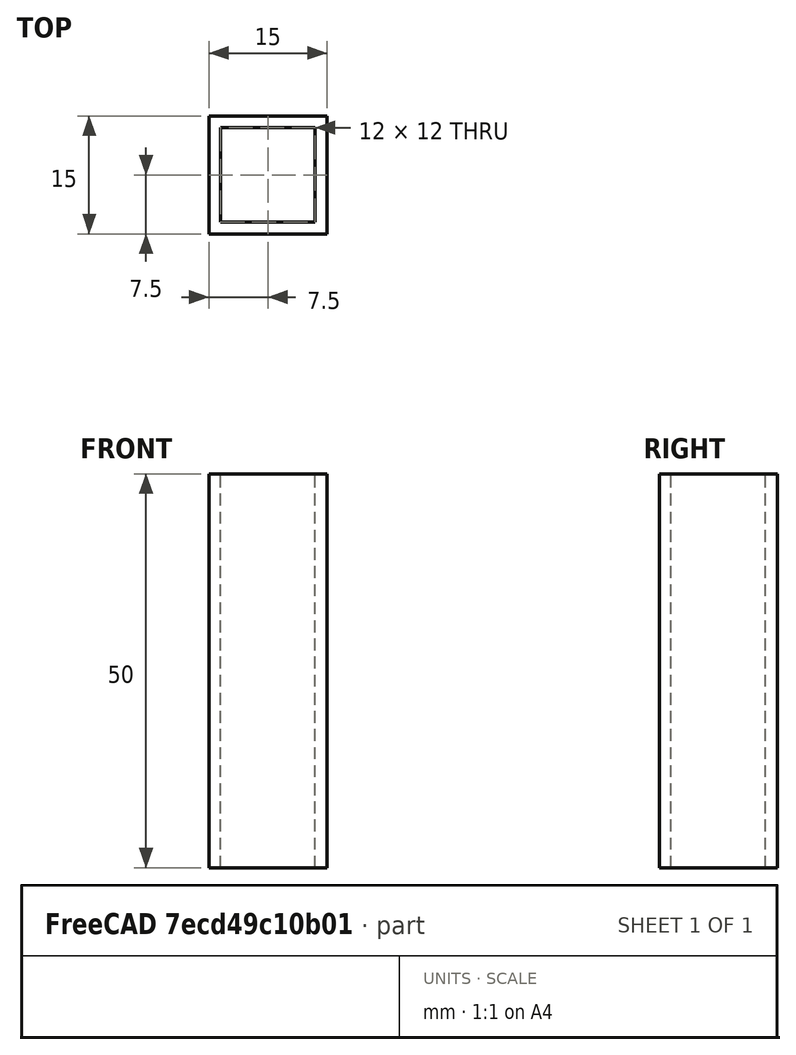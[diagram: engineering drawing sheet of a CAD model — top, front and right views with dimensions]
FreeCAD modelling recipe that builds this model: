
FCSTD DOCUMENT  (FreeCAD 0.16R6698 (Git))
Label: Tube 45
License: All rights reserved
LicenseURL: http://en.wikipedia.org/wiki/All_rights_reserved
objects: Sketcher::SketchObject×1, PartDesign::Pad×1
note: 3 computed .brp shape members not serialized (recipe doc carries the construction recipe); baked Part::Feature solids carry a one-line shape summary decoded from their .brp

FEATURE [Sketcher::SketchObject] Sketch
  sketch-geometry (8):
    g0: LineSegment StartX=-7.5 StartY=7.5 StartZ=0 EndX=7.5 EndY=7.5 EndZ=0
    g1: LineSegment StartX=7.5 StartY=7.5 StartZ=0 EndX=7.5 EndY=-7.5 EndZ=0
    g2: LineSegment StartX=7.5 StartY=-7.5 StartZ=0 EndX=-7.5 EndY=-7.5 EndZ=0
    g3: LineSegment StartX=-7.5 StartY=-7.5 StartZ=0 EndX=-7.5 EndY=7.5 EndZ=0
    g4: LineSegment StartX=-6 StartY=6 StartZ=0 EndX=6 EndY=6 EndZ=0
    g5: LineSegment StartX=6 StartY=6 StartZ=0 EndX=6 EndY=-6 EndZ=0
    g6: LineSegment StartX=6 StartY=-6 StartZ=0 EndX=-6 EndY=-6 EndZ=0
    g7: LineSegment StartX=-6 StartY=-6 StartZ=0 EndX=-6 EndY=6 EndZ=0
  constraints (24):
    c: Coincident(g0,g1)
    c: Coincident(g1,g2)
    c: Coincident(g2,g3)
    c: Coincident(g3,g0)
    c: Horizontal(g0)
    c: Horizontal(g2)
    c: Vertical(g1)
    c: Vertical(g3)
    c: Coincident(g4,g5)
    c: Coincident(g5,g6)
    c: Coincident(g6,g7)
    c: Coincident(g7,g4)
    c: Horizontal(g4)
    c: Horizontal(g6)
    c: Vertical(g5)
    c: Vertical(g7)
    c: DistanceX(g0,g0) = 15
    c: DistanceY(g3,g3) = 15
    c: DistanceY(g7,g7) = 12
    c: DistanceX(g4,g4) = 12
    c: DistanceX(g0,g4) = 1.5
    c: DistanceY(g4,g0) = 1.5
    c: DistanceX(g4,g-1) = 6
    c: DistanceY(g-1,g4) = 6
FEATURE [PartDesign::Pad] Pad
  Length = 50
  Length2 = 100
  Sketch = -> Sketch
  Type = 0
